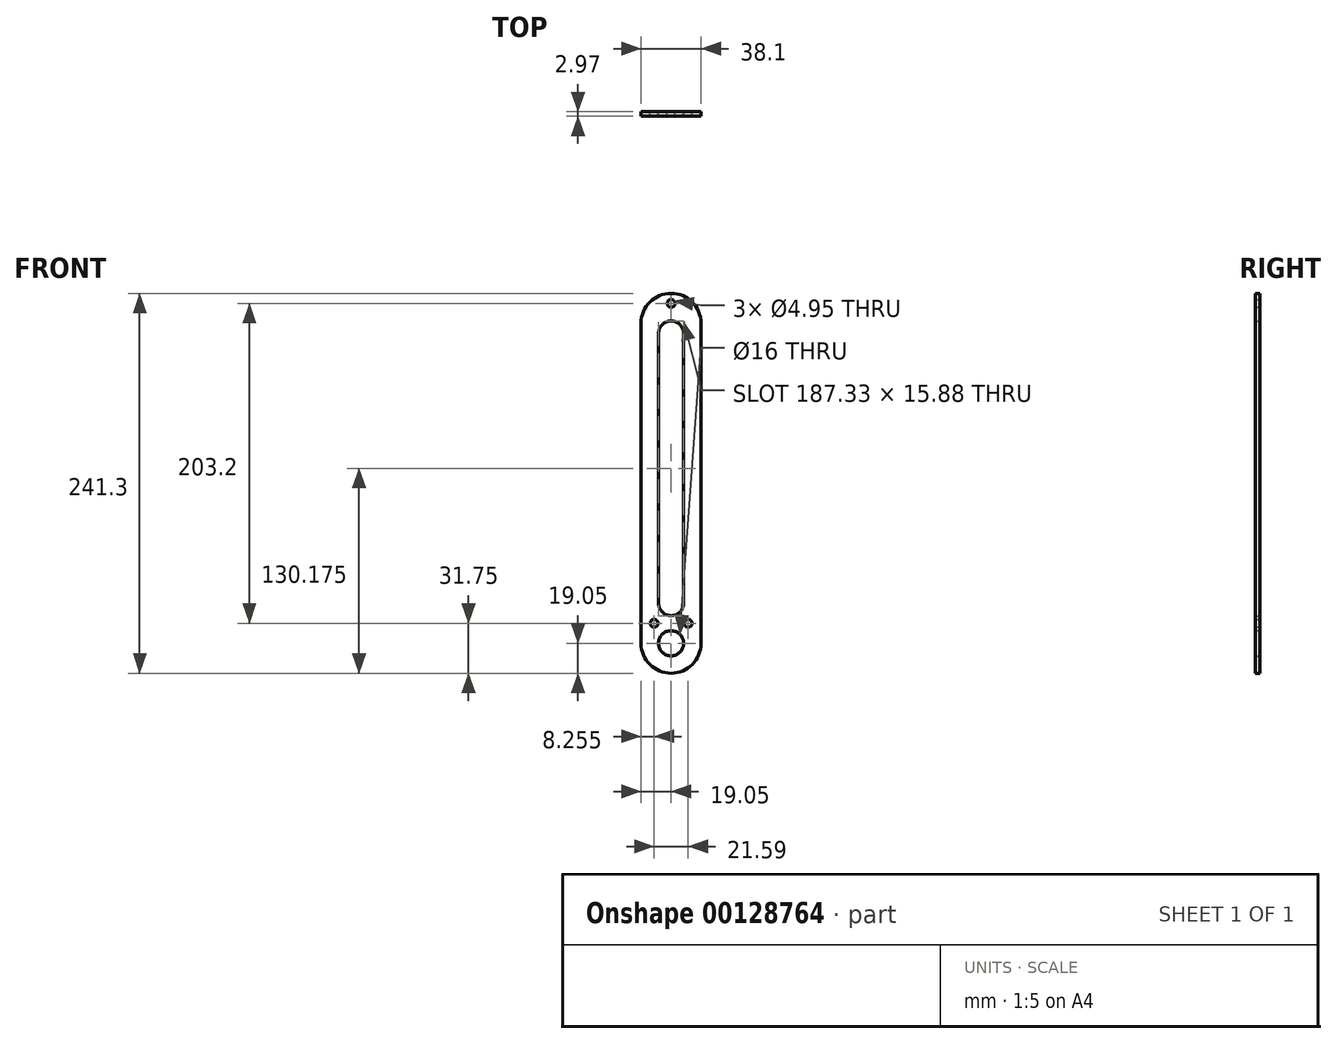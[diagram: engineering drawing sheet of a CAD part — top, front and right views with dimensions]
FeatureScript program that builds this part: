
annotation { "Feature Type Name" : "Feature", "Feature Type Description" : "" }
export const myFeature = defineFeature(function(context is Context, id is Id, definition is map)
    precondition{}
    {
        {
            var Q0;
            Q0=qCreatedBy(makeId("Front.planeOp"),FACE);
            var sketch = newSketch(context, id + "F0", { "sketchPlane" : qUnion([Q0])});
            skLineSegment(sketch, "E0", {"start": v(-19.05, -203.2) * mm, "end": v(-19.05, 0) * mm});
            skArc(sketch, "E1", {"start": v(-19.05, 0) * mm, "mid": v(0, 19.05) * mm, "end": v(19.05, 0) * mm});
            skLineSegment(sketch, "E2", {"start": v(19.05, 0) * mm, "end": v(19.05, -203.2) * mm});
            skArc(sketch, "E3", {"start": v(-19.05, -203.2) * mm, "mid": v(0, -222.25) * mm, "end": v(19.05, -203.2) * mm});
            skLineSegment(sketch, "E4", {"start": v(-7.94, -177.8) * mm, "end": v(-7.94, -6.35) * mm});
            skLineSegment(sketch, "E5", {"start": v(7.94, -177.8) * mm, "end": v(7.94, -6.35) * mm});
            skCircle(sketch, "E6", {"center": v(0, -203.2) * mm, "radius": 8 * mm});
            skArc(sketch, "E7", {"start": v(-7.94, -177.8) * mm, "mid": v(0, -185.74) * mm, "end": v(7.94, -177.8) * mm});
            skArc(sketch, "E8", {"start": v(-7.94, -6.35) * mm, "mid": v(0, 1.59) * mm, "end": v(7.94, -6.35) * mm});
            skCircle(sketch, "E9", {"center": v(-10.8, -190.5) * mm, "radius": 2.48 * mm});
            skCircle(sketch, "E10", {"center": v(10.8, -190.5) * mm, "radius": 2.48 * mm});
            skCircle(sketch, "E11", {"center": v(0, 12.7) * mm, "radius": 2.48 * mm});
            skSolve(sketch);
        }
        {
            var Q0;
            Q0=makeQuery(id+"F0.imprint","IMPRINT",FACE,{"disambiguationData":[TD([[makeQuery(id+"F0.imprint","IMPRINT",EDGE,{"derivedFrom":sQuery(id+"F0.wireOp",EDGE,"E0")}),-1.0]])]});
            extrude(context, id + "F1", {"entities" : qUnion([Q0]), "depth" : 2.97 * mm});
        }
    });
